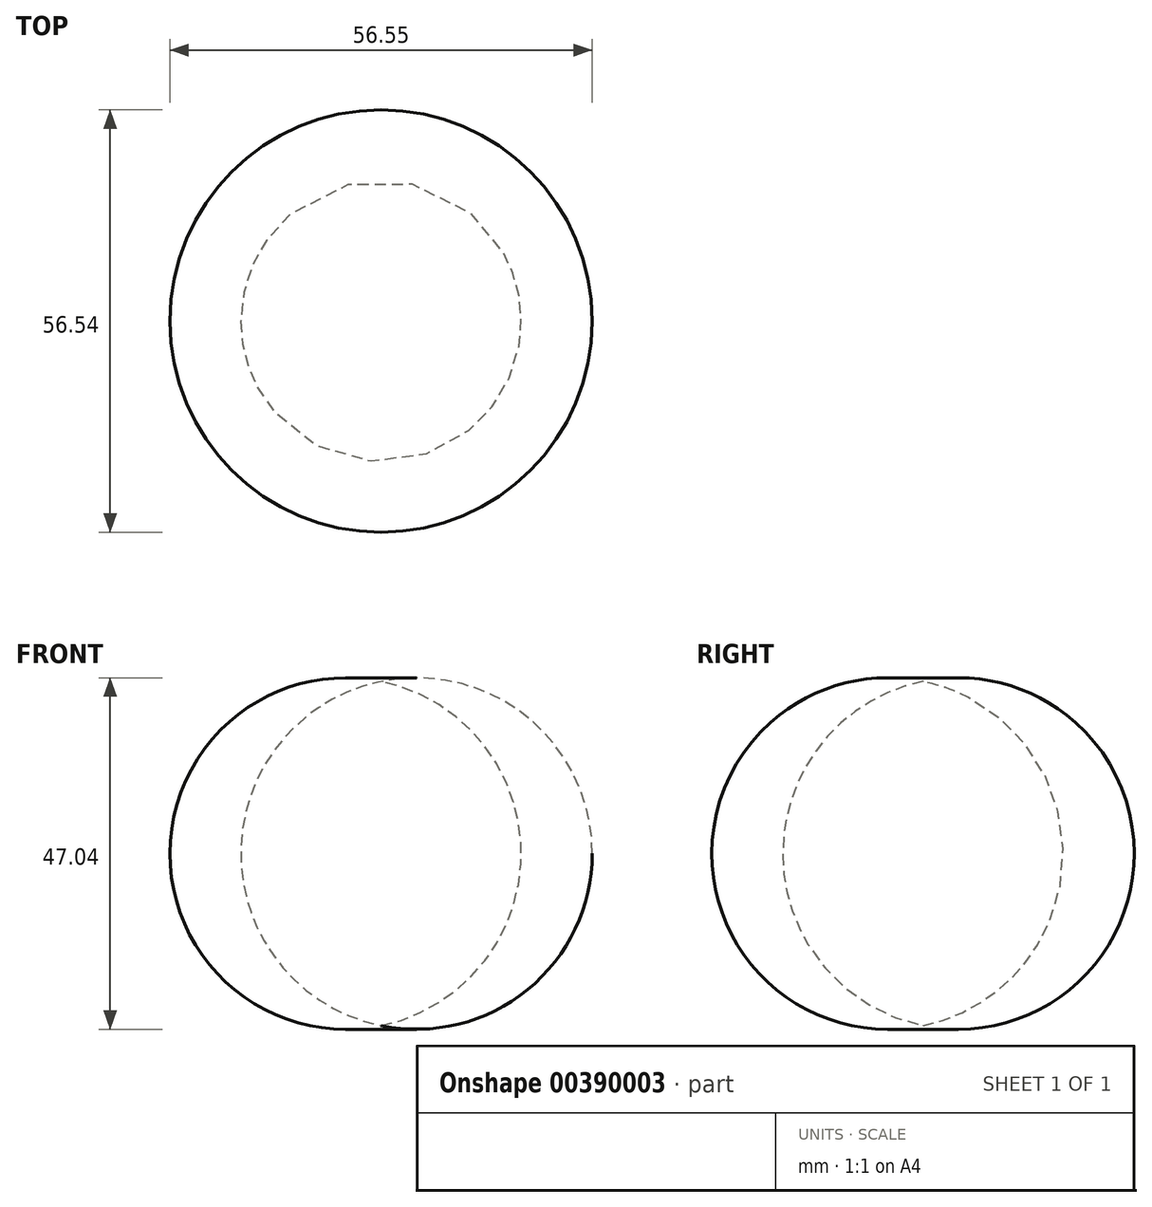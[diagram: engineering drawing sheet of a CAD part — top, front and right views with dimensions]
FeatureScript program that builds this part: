
annotation { "Feature Type Name" : "Feature", "Feature Type Description" : "" }
export const myFeature = defineFeature(function(context is Context, id is Id, definition is map)
    precondition{}
    {
        {
            var Q0;
            Q0=qCreatedBy(makeId("Front.planeOp"),FACE);
            var sketch = newSketch(context, id + "F0", { "sketchPlane" : qUnion([Q0])});
            skLineSegment(sketch, "E0", {"start": v(58.78, 61.8) * mm, "end": v(58.78, 15.74) * mm});
            skArc(sketch, "E1", {"start": v(58.78, 61.8) * mm, "mid": v(40, 38.77) * mm, "end": v(58.78, 15.74) * mm});
            skSolve(sketch);
        }
        {
            var Q0;
            Q0=makeQuery(id+"F0.imprint","IMPRINT",FACE,{"disambiguationData":[TD([[makeQuery(id+"F0.imprint","IMPRINT",EDGE,{"derivedFrom":sQuery(id+"F0.wireOp",EDGE,"E0")}),-1.0]])]});
            var Q1;
            Q1=sQuery(id+"F0.wireOp",EDGE,"E0");
            revolve(context, id + "F1", {"entities" : qUnion([Q0]), "axis" : qUnion([Q1]), "revolveType" : RevolveType.FULL});
        }
    });
